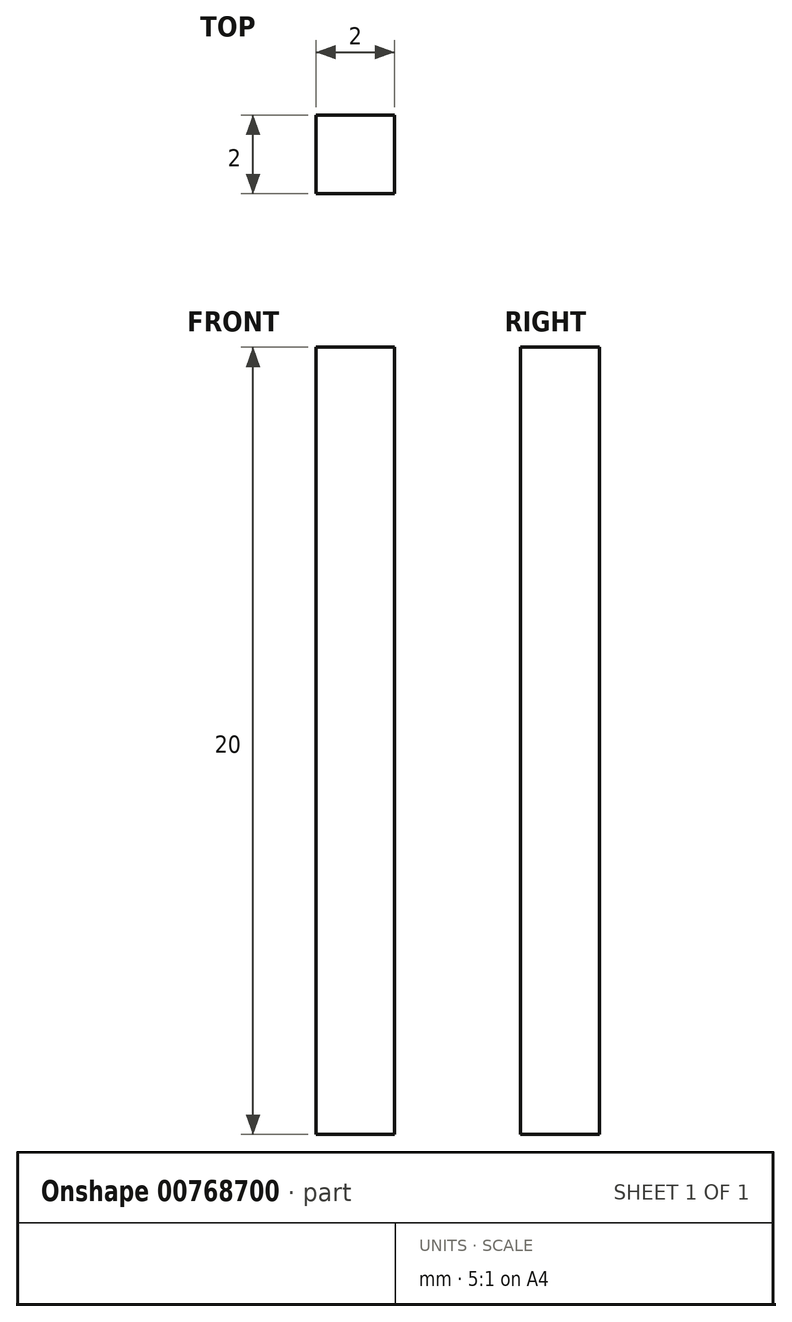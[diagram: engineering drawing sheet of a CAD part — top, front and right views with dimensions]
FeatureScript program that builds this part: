
annotation { "Feature Type Name" : "Feature", "Feature Type Description" : "" }
export const myFeature = defineFeature(function(context is Context, id is Id, definition is map)
    precondition{}
    {
        {
            var Q0;
            Q0=qCreatedBy(makeId("Top.planeOp"),FACE);
            var sketch = newSketch(context, id + "F0", { "sketchPlane" : qUnion([Q0])});
            skLineSegment(sketch, "E0.bottom", {"start": v(1, 1) * mm, "end": v(-1, 1) * mm});
            skLineSegment(sketch, "E0.top", {"start": v(1, -1) * mm, "end": v(-1, -1) * mm});
            skLineSegment(sketch, "E0.left", {"start": v(1, 1) * mm, "end": v(1, -1) * mm});
            skLineSegment(sketch, "E0.right", {"start": v(-1, 1) * mm, "end": v(-1, -1) * mm});
            skPoint(sketch, "E0.middle", {"position": v(0, 0) * mm});
            skSolve(sketch);
        }
        {
            var Q0;
            Q0 = qSketchRegion(id + "F0", true);
            extrude(context, id + "F1", {"entities" : qUnion([Q0]), "depth" : 20 * mm, "offsetDistance" : 25 * mm});
        }
    });
